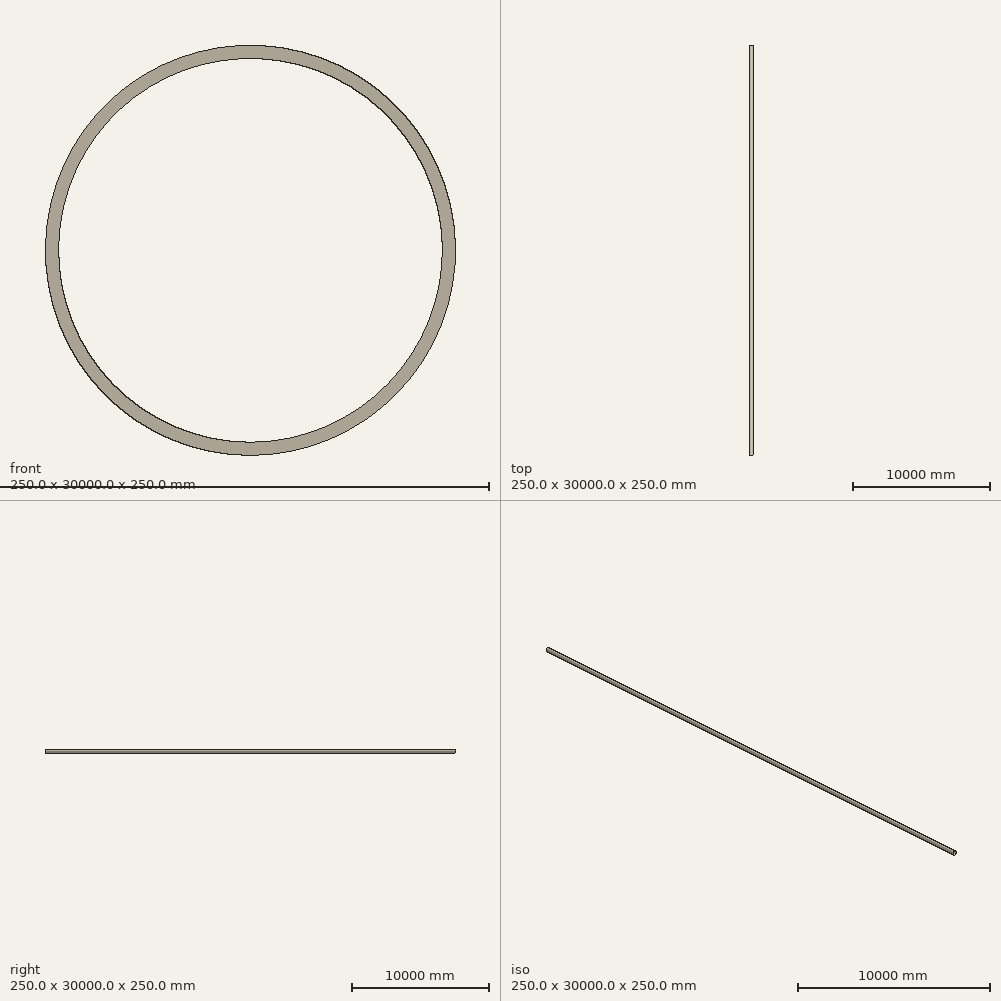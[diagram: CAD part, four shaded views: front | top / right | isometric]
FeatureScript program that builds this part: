
annotation { "Feature Type Name" : "Feature", "Feature Type Description" : "" }
export const myFeature = defineFeature(function(context is Context, id is Id, definition is map)
    precondition{}
    {
        {
            var Q0;
            Q0=qCreatedBy(makeId("Front.planeOp"),FACE);
            var sketch = newSketch(context, id + "F0", { "sketchPlane" : qUnion([Q0])});
            skCircle(sketch, "E0", {"center": v(0, 0) * mm, "radius": 125 * mm});
            skCircle(sketch, "E1", {"center": v(0, 0) * mm, "radius": 116.95 * mm});
            skSolve(sketch);
        }
        {
            var Q0;
            Q0=makeQuery(id+"F0.imprint","IMPRINT",FACE,{"disambiguationData":[TD([[makeQuery(id+"F0.imprint","IMPRINT",EDGE,{"derivedFrom":sQuery(id+"F0.wireOp",EDGE,"E0")}),1.0]])]});
            extrude(context, id + "F1", {"entities" : qUnion([Q0]), "endBound" : BoundingType.SYMMETRIC, "depth" : 30000 * mm});
        }
    });
